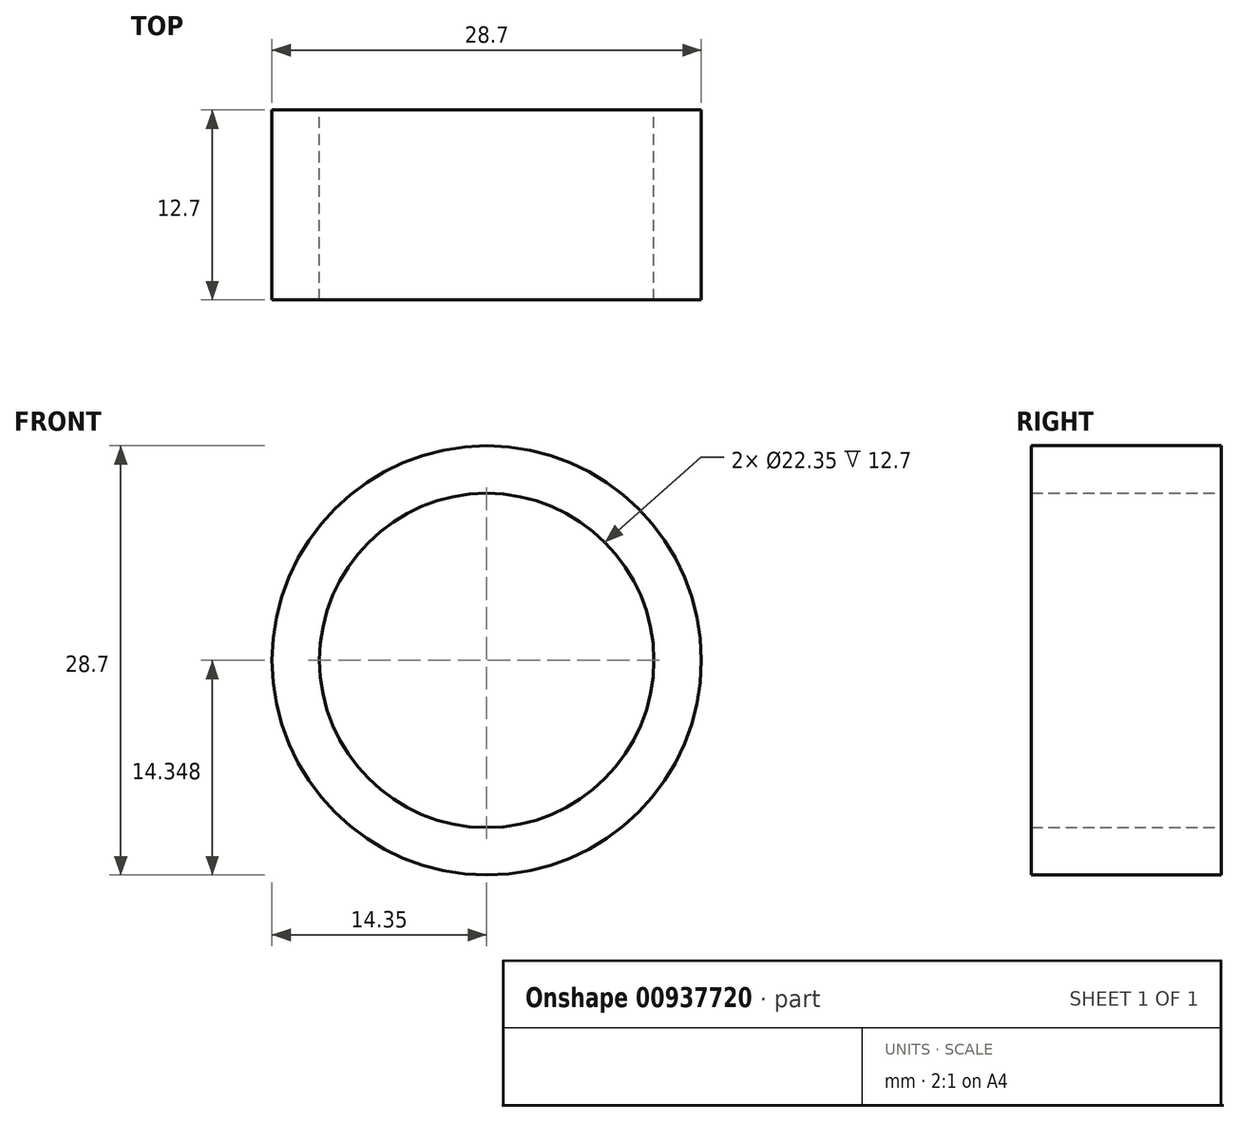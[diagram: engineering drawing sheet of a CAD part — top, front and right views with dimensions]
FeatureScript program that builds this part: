
annotation { "Feature Type Name" : "Feature", "Feature Type Description" : "" }
export const myFeature = defineFeature(function(context is Context, id is Id, definition is map)
    precondition{}
    {
        {
            var Q0;
            Q0=qCreatedBy(makeId("Front.planeOp"),FACE);
            var sketch = newSketch(context, id + "F0", { "sketchPlane" : qUnion([Q0])});
            skCircle(sketch, "E0", {"center": v(-32.68, 34.07) * mm, "radius": 11.18 * mm});
            skCircle(sketch, "E1.0", {"center": v(-32.68, 34.07) * mm, "radius": 14.35 * mm});
            skSolve(sketch);
        }
        {
            var Q0;
            Q0=makeQuery(id+"F0.imprint","IMPRINT",FACE,{"disambiguationData":[TD([[makeQuery(id+"F0.imprint","IMPRINT",EDGE,{"derivedFrom":sQuery(id+"F0.wireOp",EDGE,"E0")}),-1.0]])]});
            extrude(context, id + "F1", {"entities" : qUnion([Q0]), "depth" : 12.7 * mm, "offsetDistance" : 25.4 * mm});
        }
    });
